# Revit family: xTowel_Bar-American_Standard-C_Series-8337_Series
name_source: partatom
category: Specialty Equipment
revit_build: Autodesk Revit 2014 (Build: 20130308_1515(x64)
units: mm (PartAtom-declared; Revit-internal decimal feet)

## types (2) — shared parameters
Assembly Code = C1030220
Default Elevation = 40"
Finish = Metal-American Standard-002-Polished Chrome
Height = 2"
Installation Type = Wall Mounted
Length = 4 11/16"
Manufacturer = American Standard
Material = Metal-American Standard-002-Polished Chrome
Price = Prices may vary. Please consult Manufacturer Representative for most up-to-date price list.
Product Documentation Link = https://www.americanstandard-us.com
Product Page URL = https://www.americanstandard-us.com
Revised Date = 11/22/2016
URL = http://www.americanstandard-us.com
Warranty Information = 1 Year Warranty

## per-type parameters (varying)
| type | Description | Width |
| 8337.024 | C Series 24" Towel Bar. | 24" |
| 8337.018 | C Series 18" Towel Bar. | 18" |

note: column(s) folded — value = type name in every type: Model

## geometry (parser evidence)
native form markers: Sweep x3
no freeform markers — native parametric forms only
